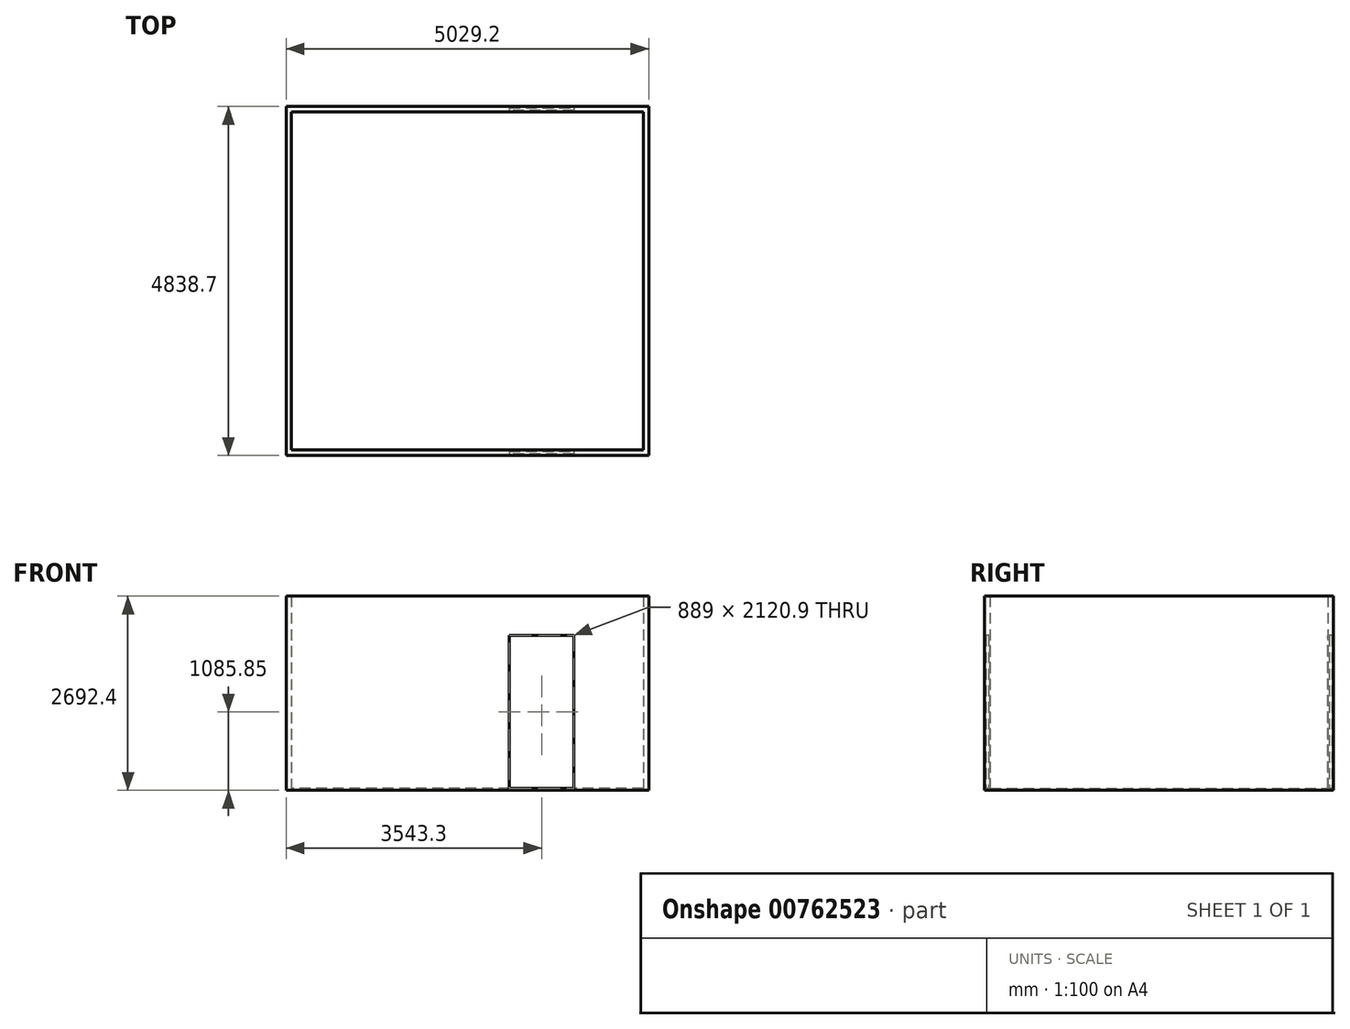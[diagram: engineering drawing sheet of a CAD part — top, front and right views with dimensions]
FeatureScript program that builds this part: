
annotation { "Feature Type Name" : "Feature", "Feature Type Description" : "" }
export const myFeature = defineFeature(function(context is Context, id is Id, definition is map)
    precondition{}
    {
        {
            var Q0;
            Q0=qCreatedBy(makeId("Top.planeOp"),FACE);
            var sketch = newSketch(context, id + "F0", { "sketchPlane" : qUnion([Q0])});
            skLineSegment(sketch, "E0", {"start": v(2438.4, -2343.15) * mm, "end": v(-2438.4, -2343.15) * mm});
            skLineSegment(sketch, "E1", {"start": v(-2438.4, -2343.15) * mm, "end": v(-2438.4, 2343.15) * mm});
            skLineSegment(sketch, "E2", {"start": v(-2438.4, 2343.15) * mm, "end": v(2438.4, 2343.15) * mm});
            skLineSegment(sketch, "E3", {"start": v(2438.4, -2343.15) * mm, "end": v(2438.4, 2343.15) * mm});
            skSolve(sketch);
        }
        {
            var Q0;
            Q0 = qSketchRegion(id + "F0", true);
            extrude(context, id + "F1", {"entities" : qUnion([Q0]), "depth" : 25.4 * mm, "offsetDistance" : 25.4 * mm});
        }
        {
            var Q0;
            Q0=makeQuery(id+"F1.opExtrude","CAP_FACE",FACE,{"disambiguationData":[OSD([sQuery(id+"F0.wireOp",EDGE,"E0"),sQuery(id+"F0.wireOp",EDGE,"E1"),sQuery(id+"F0.wireOp",EDGE,"E2"),sQuery(id+"F0.wireOp",EDGE,"E3")])],"isStart":false});
            var sketch = newSketch(context, id + "F2", { "sketchPlane" : qUnion([Q0])});
            skLineSegment(sketch, "E4.0", {"start": v(-2438.4, -2343.15) * mm, "end": v(2438.4, -2343.15) * mm});
            skLineSegment(sketch, "E4.1", {"start": v(-2438.4, 2343.15) * mm, "end": v(-2438.4, -2343.15) * mm});
            skLineSegment(sketch, "E4.2", {"start": v(2438.4, 2343.15) * mm, "end": v(-2438.4, 2343.15) * mm});
            skLineSegment(sketch, "E4.3", {"start": v(2438.4, -2343.15) * mm, "end": v(2438.4, 2343.15) * mm});
            skLineSegment(sketch, "E5.0", {"start": v(-2514.6, -2419.35) * mm, "end": v(2514.6, -2419.35) * mm});
            skLineSegment(sketch, "E5.1", {"start": v(-2514.6, 2419.35) * mm, "end": v(-2514.6, -2419.35) * mm});
            skLineSegment(sketch, "E5.2", {"start": v(2514.6, 2419.35) * mm, "end": v(-2514.6, 2419.35) * mm});
            skLineSegment(sketch, "E5.3", {"start": v(2514.6, -2419.35) * mm, "end": v(2514.6, 2419.35) * mm});
            skSolve(sketch);
        }
        {
            var Q0;
            Q0 = qSketchRegion(id + "F2", true);
            extrude(context, id + "F3", {"entities" : qUnion([Q0]), "depth" : 2667 * mm, "offsetDistance" : 25.4 * mm});
        }
        {
            var Q0;
            Q0=makeQuery(id+"F3.opExtrude","SWEPT_FACE",FACE,{"disambiguationData":[OSD([sQuery(id+"F2.wireOp",EDGE,"E5.0")])]});
            var sketch = newSketch(context, id + "F4", { "sketchPlane" : qUnion([Q0])});
            skLineSegment(sketch, "E6", {"start": v(1473.2, 25.4) * mm, "end": v(1473.2, 2146.3) * mm});
            skLineSegment(sketch, "E7", {"start": v(1473.2, 2146.3) * mm, "end": v(584.2, 2146.3) * mm});
            skLineSegment(sketch, "E8", {"start": v(584.2, 2146.3) * mm, "end": v(584.2, 25.4) * mm});
            skLineSegment(sketch, "E9", {"start": v(1473.2, 25.4) * mm, "end": v(584.2, 25.4) * mm});
            skSolve(sketch);
        }
        {
            var Q0;
            Q0 = qSketchRegion(id + "F4", true);
            extrude(context, id + "F5", {"entities" : qUnion([Q0]), "operationType" : NewBodyOperationType.REMOVE, "endBound" : BoundingType.THROUGH_ALL, "oppositeDirection" : true, "depth" : 25.4 * mm, "offsetDistance" : 25.4 * mm});
        }
        {
            var Q0;
            Q0=makeQuery(id+"F1.opExtrude","CAP_FACE",FACE,{"disambiguationData":[OSD([sQuery(id+"F0.wireOp",EDGE,"E0"),sQuery(id+"F0.wireOp",EDGE,"E1"),sQuery(id+"F0.wireOp",EDGE,"E2"),sQuery(id+"F0.wireOp",EDGE,"E3")])],"isStart":true});
            var sketch = newSketch(context, id + "F6", { "sketchPlane" : qUnion([Q0])});
            skLineSegment(sketch, "E10.0", {"start": v(2438.4, 2343.15) * mm, "end": v(-2438.4, 2343.15) * mm});
            skLineSegment(sketch, "E10.1", {"start": v(2438.4, -2343.15) * mm, "end": v(2438.4, 2343.15) * mm});
            skLineSegment(sketch, "E10.2", {"start": v(-2438.4, -2343.15) * mm, "end": v(2438.4, -2343.15) * mm});
            skLineSegment(sketch, "E10.3", {"start": v(-2438.4, 2343.15) * mm, "end": v(-2438.4, -2343.15) * mm});
            skLineSegment(sketch, "E11.0", {"start": v(2514.6, 2419.35) * mm, "end": v(-2514.6, 2419.35) * mm});
            skLineSegment(sketch, "E11.1", {"start": v(2514.6, -2419.35) * mm, "end": v(2514.6, 2419.35) * mm});
            skLineSegment(sketch, "E11.2", {"start": v(-2514.6, -2419.35) * mm, "end": v(2514.6, -2419.35) * mm});
            skLineSegment(sketch, "E11.3", {"start": v(-2514.6, 2419.35) * mm, "end": v(-2514.6, -2419.35) * mm});
            skSolve(sketch);
        }
        {
            var Q0;
            Q0 = qSketchRegion(id + "F6", true);
            extrude(context, id + "F7", {"entities" : qUnion([Q0]), "operationType" : NewBodyOperationType.ADD, "oppositeDirection" : true, "depth" : 25.4 * mm, "offsetDistance" : 25.4 * mm});
        }
        {
            var Q0;
            Q0=makeQuery(id+"F7.boolean.opBoolean","MERGE",FACE,{"derivedFrom":[makeQuery(id+"F1.opExtrude","CAP_FACE",FACE,{"disambiguationData":[OSD([sQuery(id+"F0.wireOp",EDGE,"E0"),sQuery(id+"F0.wireOp",EDGE,"E1"),sQuery(id+"F0.wireOp",EDGE,"E2"),sQuery(id+"F0.wireOp",EDGE,"E3")])],"isStart":false}),makeQuery(id+"F7.opExtrude","CAP_FACE",FACE,{"disambiguationData":[OSD([sQuery(id+"F6.wireOp",EDGE,"E10.0"),sQuery(id+"F6.wireOp",EDGE,"E10.1"),sQuery(id+"F6.wireOp",EDGE,"E10.2"),sQuery(id+"F6.wireOp",EDGE,"E10.3"),sQuery(id+"F6.wireOp",EDGE,"E11.0"),sQuery(id+"F6.wireOp",EDGE,"E11.1"),sQuery(id+"F6.wireOp",EDGE,"E11.2"),sQuery(id+"F6.wireOp",EDGE,"E11.3")])],"isStart":false})]});
            var sketch = newSketch(context, id + "F8", { "sketchPlane" : qUnion([Q0])});
            skLineSegment(sketch, "E12", {"start": v(584.2, -2362.2) * mm, "end": v(1473.2, -2362.2) * mm});
            skLineSegment(sketch, "E13", {"start": v(1473.2, -2400.3) * mm, "end": v(584.2, -2400.3) * mm});
            skLineSegment(sketch, "E14", {"start": v(584.2, -2381.25) * mm, "end": v(1473.2, -2381.25) * mm, "construction": true});
            skLineSegment(sketch, "E15", {"start": v(1473.2, -2400.3) * mm, "end": v(1473.2, -2362.2) * mm});
            skLineSegment(sketch, "E16", {"start": v(584.2, -2400.3) * mm, "end": v(584.2, -2362.2) * mm});
            skLineSegment(sketch, "E17", {"start": v(584.2, 2400.3) * mm, "end": v(1473.2, 2400.3) * mm});
            skLineSegment(sketch, "E18", {"start": v(1473.2, 2362.2) * mm, "end": v(584.2, 2362.2) * mm});
            skLineSegment(sketch, "E19", {"start": v(584.2, 2381.25) * mm, "end": v(1473.2, 2381.25) * mm, "construction": true});
            skLineSegment(sketch, "E20", {"start": v(1473.2, 2362.2) * mm, "end": v(1473.2, 2400.3) * mm});
            skLineSegment(sketch, "E21", {"start": v(584.2, 2362.2) * mm, "end": v(584.2, 2400.3) * mm});
            skSolve(sketch);
        }
        {
            var Q0;
            Q0 = qSketchRegion(id + "F8", true);
            extrude(context, id + "F9", {"entities" : qUnion([Q0]), "depth" : 2120.9 * mm, "offsetDistance" : 25.4 * mm});
        }
    });
